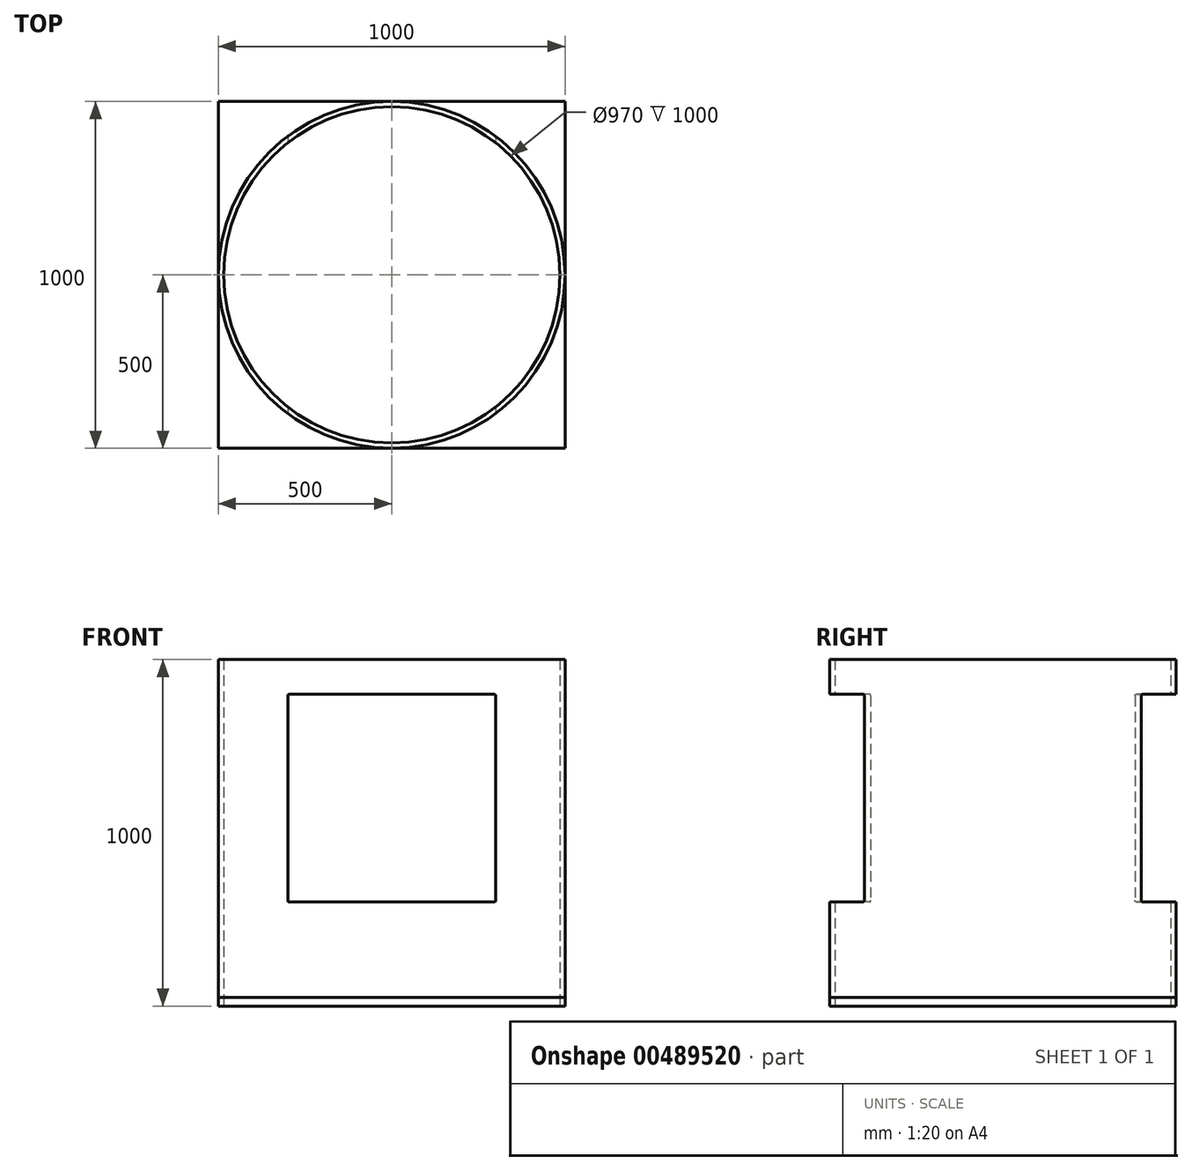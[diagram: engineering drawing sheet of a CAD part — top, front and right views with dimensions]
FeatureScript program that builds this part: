
annotation { "Feature Type Name" : "Feature", "Feature Type Description" : "" }
export const myFeature = defineFeature(function(context is Context, id is Id, definition is map)
    precondition{}
    {
        {
            var Q0;
            Q0=qCreatedBy(makeId("Top.planeOp"),FACE);
            var sketch = newSketch(context, id + "F0", { "sketchPlane" : qUnion([Q0])});
            skCircle(sketch, "E0", {"center": v(0, 0) * mm, "radius": 500 * mm});
            skCircle(sketch, "E1", {"center": v(0, 0) * mm, "radius": 485 * mm});
            skCircle(sketch, "E2", {"center": v(0, 0) * mm, "radius": 226.54 * mm});
            skSolve(sketch);
        }
        {
            var Q0;
            Q0=makeQuery(id+"F0.imprint","IMPRINT",FACE,{"disambiguationData":[TD([[makeQuery(id+"F0.imprint","IMPRINT",EDGE,{"derivedFrom":sQuery(id+"F0.wireOp",EDGE,"E0")}),1.0]])]});
            var sketch = newSketch(context, id + "F1", { "sketchPlane" : qUnion([Q0])});
            skSolve(sketch);
        }
        {
            var Q0;
            Q0=makeQuery(id+"F0.imprint","IMPRINT",FACE,{"disambiguationData":[TD([[makeQuery(id+"F0.imprint","IMPRINT",EDGE,{"derivedFrom":sQuery(id+"F0.wireOp",EDGE,"E0")}),1.0]])]});
            var Q1;
            Q1=sQuery(id+"F0.wireOp",EDGE,"E2");
            var Q2;
            Q2=sQuery(id+"F0.wireOp",EDGE,"E1");
            var Q3;
            Q3=sQuery(id+"F0.wireOp",EDGE,"E0");
            extrude(context, id + "F2", {"entities" : qUnion([Q0]), "surfaceEntities" : qUnion([Q1, Q2, Q3]), "depth" : 1000 * mm});
        }
        {
            var Q0;
            Q0=makeQuery(id+"F1.imprint","IMPRINT",FACE,{"disambiguationData":[TD([[makeQuery(id+"F1.imprint","IMPRINT",EDGE,{"derivedFrom":makeQuery(id+"F0.imprint","IMPRINT",EDGE,{"derivedFrom":sQuery(id+"F0.wireOp",EDGE,"E0")})}),1.0]])]});
            var sketch = newSketch(context, id + "F3", { "sketchPlane" : qUnion([Q0])});
            skLineSegment(sketch, "E3.bottom", {"start": v(-500, -500) * mm, "end": v(500, -500) * mm});
            skLineSegment(sketch, "E3.top", {"start": v(-500, 500) * mm, "end": v(500, 500) * mm});
            skLineSegment(sketch, "E3.left", {"start": v(-500, -500) * mm, "end": v(-500, 500) * mm});
            skLineSegment(sketch, "E3.right", {"start": v(500, -500) * mm, "end": v(500, 500) * mm});
            skSolve(sketch);
        }
        {
            var Q0;
            Q0=qCreatedBy(makeId("Front.planeOp"),FACE);
            var sketch = newSketch(context, id + "F4", { "sketchPlane" : qUnion([Q0])});
            skLineSegment(sketch, "E4.bottom", {"start": v(-295, 900) * mm, "end": v(295, 900) * mm});
            skLineSegment(sketch, "E4.top", {"start": v(-295, 300) * mm, "end": v(295, 300) * mm});
            skLineSegment(sketch, "E4.left", {"start": v(-300, 895) * mm, "end": v(-300, 305) * mm});
            skLineSegment(sketch, "E4.right", {"start": v(300, 895) * mm, "end": v(300, 305) * mm});
            skPoint(sketch, "E5.visualSharp", {"position": v(-300, 300) * mm});
            skArc(sketch, "E5.filletArc", {"start": v(-300, 305) * mm, "mid": v(-298.54, 301.46) * mm, "end": v(-295, 300) * mm});
            skPoint(sketch, "E6.visualSharp", {"position": v(300, 300) * mm});
            skArc(sketch, "E6.filletArc", {"start": v(295, 300) * mm, "mid": v(298.54, 301.46) * mm, "end": v(300, 305) * mm});
            skPoint(sketch, "E7.visualSharp", {"position": v(300, 900) * mm});
            skArc(sketch, "E7.filletArc", {"start": v(300, 895) * mm, "mid": v(298.54, 898.54) * mm, "end": v(295, 900) * mm});
            skPoint(sketch, "E8.visualSharp", {"position": v(-300, 900) * mm});
            skArc(sketch, "E8.filletArc", {"start": v(-295, 900) * mm, "mid": v(-298.54, 898.54) * mm, "end": v(-300, 895) * mm});
            skSolve(sketch);
        }
        {
            var Q0;
            Q0 = qSketchRegion(id + "F4", true);
            extrude(context, id + "F5", {"entities" : qUnion([Q0]), "operationType" : NewBodyOperationType.REMOVE, "endBound" : BoundingType.SYMMETRIC, "oppositeDirection" : true, "depth" : 1000 * mm});
        }
        {
            var Q0;
            Q0 = qSketchRegion(id + "F3", true);
            extrude(context, id + "F6", {"entities" : qUnion([Q0]), "depth" : 25 * mm});
        }
    });
